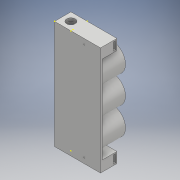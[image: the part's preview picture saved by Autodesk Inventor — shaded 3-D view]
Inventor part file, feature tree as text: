
AUTODESK INVENTOR PART (.ipt)
format: ipt  version: 2018 (Build 220112000, 112)  size: 292,864 bytes
history: native  units: mm
features: sketch x24, extrude x16, fillet x2
ambient origin geometry x8: Origin, YZ Plane, XZ Plane, XY Plane, X Axis, Y Axis, Z Axis, Center Point
bodies: Solid1 (feature_tree)
feature tree (42):
  extrude  "Extrusion1"  Depth=165.0mm
  extrude  "Extrusion2"  Depth=7.0mm
  sketch  "Sketch3"  dims[d5=7.0mm d6=22.0mm d7=0.0mm]
  extrude  "Extrusion3"  Depth=22.0mm TaperAngle=0.0deg
  extrude  "Extrusion4"  Depth=5.0mm TaperAngle=0.0deg
  extrude  "Extrusion5"  Depth=10.0mm
  sketch  "Sketch7"  dims[d18=7.5mm d19=0.0mm d20=2.0mm]
  sketch  "Sketch8"  dims[d21=3.0mm d22=45.0mm d23=0.0mm]
  extrude  "Extrusion6"  Depth=5.0mm
  fillet  "Fillet1"  Radius=5.0mm
  extrude  "Extrusion7"  Depth=2.0mm
  extrude  "Extrusion8"  Depth=45.0mm TaperAngle=0.0deg
  sketch  "Sketch12"  dims[d31=16.0mm d32=22.0mm d33=0.0mm]
  extrude  "Extrusion9"  Depth=38.65mm
  sketch  "Sketch14"  dims[d37=3.25mm d38=3.5mm d39=12.25mm]
  sketch  "Sketch15"  dims[d40=3.25mm d41=40.0mm d42=0.0mm]
  extrude  "Extrusion10"  Depth=38.65mm
  extrude  "Extrusion11"  Depth=16.0mm
  extrude  "Extrusion12"  Depth=22.0mm TaperAngle=0.0deg
  sketch  "Sketch17"  dims[d46=1.5mm]
  sketch  "Sketch18"  dims[d47=25.0mm d48=0.0mm]
  sketch  "Sketch19"  dims[d49=25.0mm]
  extrude  "Extrusion13"  Depth=12.25mm
  sketch  "Sketch21"  dims[d51=25.0mm d52=0.0mm]
  extrude  "Extrusion14"  Depth=3.5mm
  fillet  "Fillet2"  Radius=12.25mm
  extrude  "Extrusion15"  Depth=40.0mm TaperAngle=0.0deg
  extrude  "Extrusion16"  Depth=25.0mm
  sketch  "Sketch1"  dims[d0=25.0mm d1=165.0mm]
  sketch  "Sketch2"  dims[d2=3.0mm d3=0.0mm d4=7.0mm]
  sketch  "Sketch4"  dims[d8=13.0mm d9=5.0mm d10=0.0mm]
  sketch  "Sketch5"  dims[d11=5.0mm d12=0.0mm d13=10.0mm]
  sketch  "Sketch6"  dims[d14=165.0mm d15=0.0mm d16=5.0mm d17=5.0mm]
  sketch  "Sketch9"  dims[d24=42.0mm d25=38.65mm]
  sketch  "Sketch10"  dims[d26=38.65mm d27=38.65mm]
  sketch  "Sketch11"  dims[d28=45.0mm d29=0.0mm d30=16.0mm]
  sketch  "Sketch13"  dims[d35=3.5mm d36=12.25mm]
  sketch  "Sketch16"  dims[d43=40.0mm d44=0.0mm d45=25.0mm]
  sketch  "Sketch20"  dims[d50=1.5mm]
  sketch  "Sketch22"  dims[d53=2.0mm]
  sketch  "Sketch23"  dims[d54=1.0mm]
  sketch  "Sketch24"  dims[d55=5.25mm d56=0.0mm d57=1.0mm d58=1.0mm d59=5.25mm d60=0.0mm d61=10.0mm d62=0.0mm]
